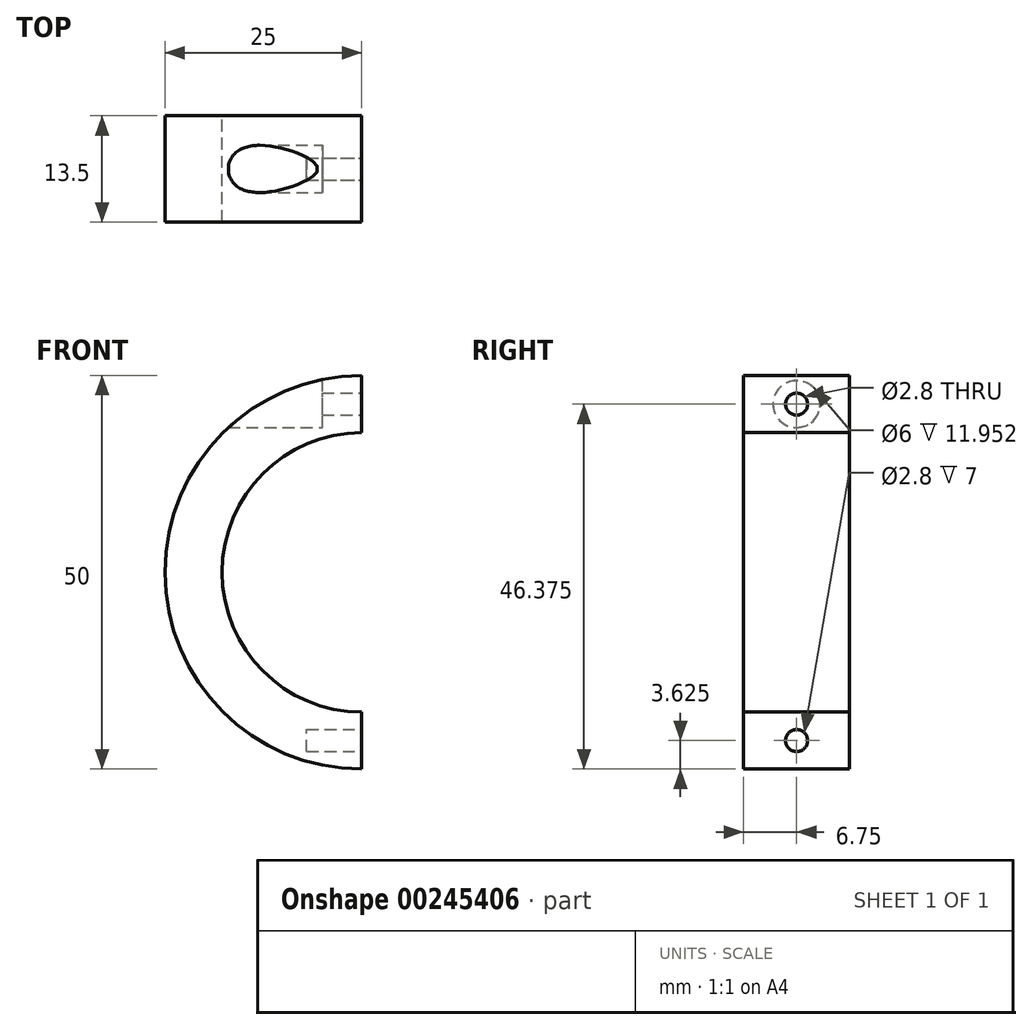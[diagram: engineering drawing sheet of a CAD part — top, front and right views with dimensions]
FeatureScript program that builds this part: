
annotation { "Feature Type Name" : "Feature", "Feature Type Description" : "" }
export const myFeature = defineFeature(function(context is Context, id is Id, definition is map)
    precondition{}
    {
        {
            var Q0;
            Q0=qCreatedBy(makeId("Front.planeOp"),FACE);
            var sketch = newSketch(context, id + "F0", { "sketchPlane" : qUnion([Q0])});
            skArc(sketch, "E0", {"start": v(0, 17.75) * mm, "mid": v(-17.75, 0) * mm, "end": v(0, -17.75) * mm});
            skArc(sketch, "E1", {"start": v(0, 25) * mm, "mid": v(-25, 0) * mm, "end": v(0, -25) * mm});
            skLineSegment(sketch, "E2", {"start": v(0, 17.75) * mm, "end": v(0, 25) * mm});
            skLineSegment(sketch, "E3", {"start": v(0, -17.75) * mm, "end": v(0, -25) * mm});
            skSolve(sketch);
        }
        {
            var Q0;
            Q0 = qSketchRegion(id + "F0", true);
            extrude(context, id + "F1", {"entities" : qUnion([Q0]), "depth" : 13.5 * mm});
        }
        {
            var Q0;
            Q0=makeQuery(id+"F1.opExtrude","SWEPT_FACE",FACE,{"disambiguationData":[OSD([sQuery(id+"F0.wireOp",EDGE,"E2")])]});
            var sketch = newSketch(context, id + "F2", { "sketchPlane" : qUnion([Q0])});
            skLineSegment(sketch, "E4", {"start": v(-6.75, 25) * mm, "end": v(-6.75, 17.75) * mm});
            skCircle(sketch, "E5", {"center": v(-6.75, 21.38) * mm, "radius": 1.4 * mm});
            skSolve(sketch);
        }
        {
            var Q0;
            Q0 = qSketchRegion(id + "F2", true);
            extrude(context, id + "F3", {"entities" : qUnion([Q0]), "operationType" : NewBodyOperationType.REMOVE, "oppositeDirection" : true, "depth" : 5 * mm});
        }
        {
            var Q0;
            Q0=makeQuery(id+"F3.boolean.opBoolean","COPY",FACE,{"derivedFrom":makeQuery(id+"F3.opExtrude","CAP_FACE",FACE,{"disambiguationData":[OSD([sQuery(id+"F2.wireOp",EDGE,"E5")])],"isStart":false})});
            var sketch = newSketch(context, id + "F4", { "sketchPlane" : qUnion([Q0])});
            skCircle(sketch, "E6", {"center": v(-6.75, 21.38) * mm, "radius": 3 * mm});
            skSolve(sketch);
        }
        {
            var Q0;
            Q0 = qSketchRegion(id + "F4", true);
            extrude(context, id + "F5", {"entities" : qUnion([Q0]), "operationType" : NewBodyOperationType.REMOVE, "oppositeDirection" : true, "depth" : 25 * mm});
        }
        {
            var Q0;
            Q0=makeQuery(id+"F1.opExtrude","SWEPT_FACE",FACE,{"disambiguationData":[OSD([sQuery(id+"F0.wireOp",EDGE,"E3")])]});
            var sketch = newSketch(context, id + "F6", { "sketchPlane" : qUnion([Q0])});
            skLineSegment(sketch, "E7", {"start": v(-6.75, -17.75) * mm, "end": v(-6.75, -25) * mm});
            skCircle(sketch, "E8", {"center": v(-6.75, -21.38) * mm, "radius": 1.4 * mm});
            skSolve(sketch);
        }
        {
            var Q0;
            Q0 = qSketchRegion(id + "F6", true);
            extrude(context, id + "F7", {"entities" : qUnion([Q0]), "operationType" : NewBodyOperationType.REMOVE, "oppositeDirection" : true, "depth" : 7 * mm});
        }
    });
